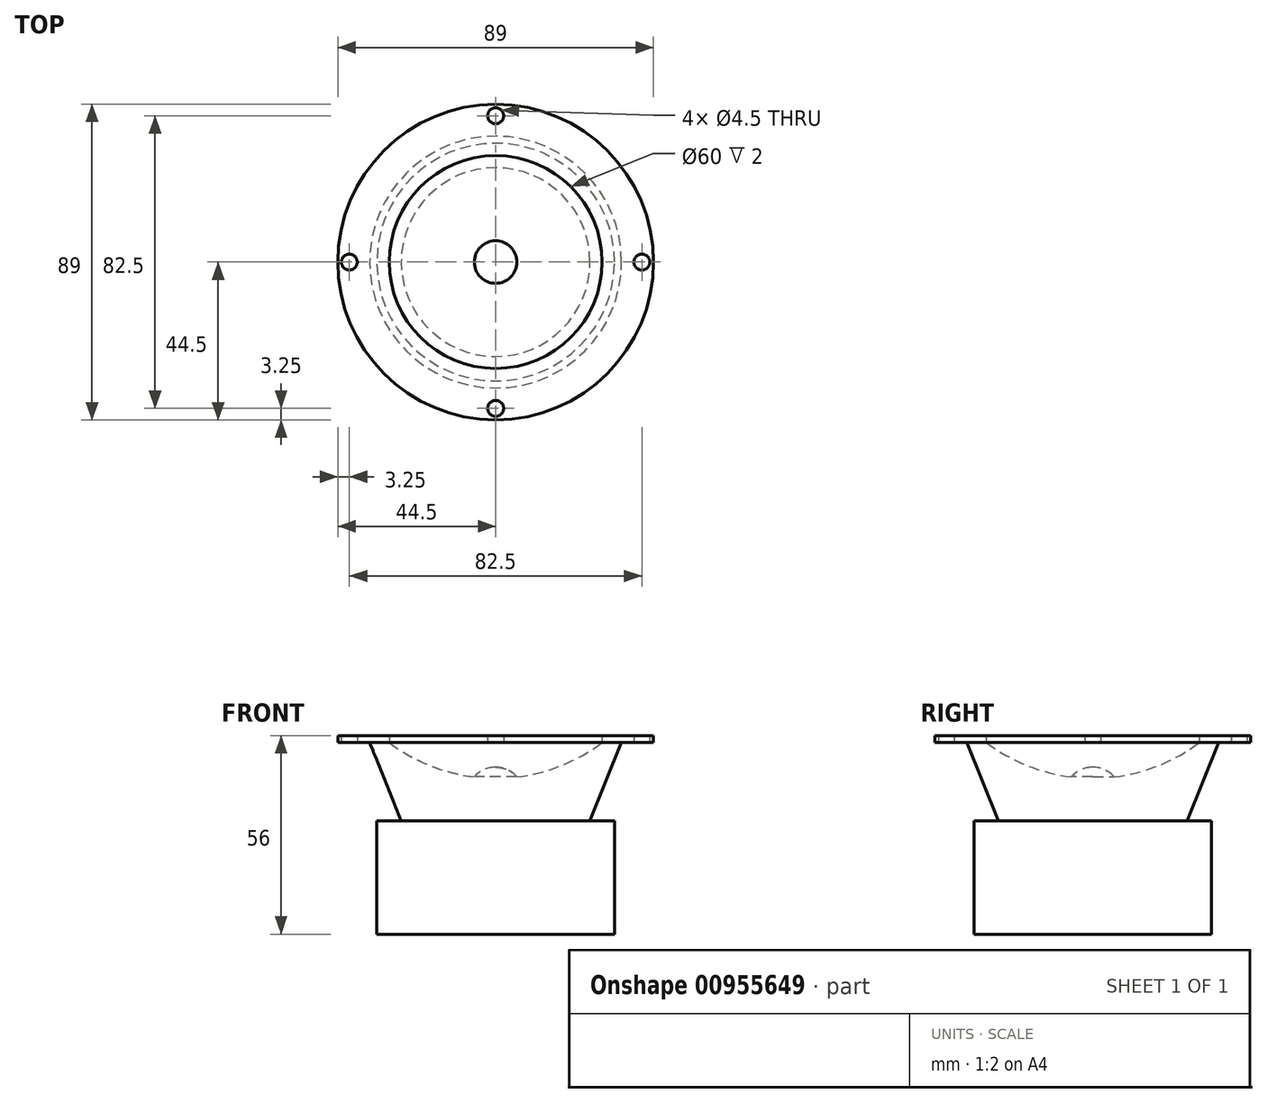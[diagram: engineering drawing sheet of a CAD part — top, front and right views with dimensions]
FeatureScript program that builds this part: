
annotation { "Feature Type Name" : "Feature", "Feature Type Description" : "" }
export const myFeature = defineFeature(function(context is Context, id is Id, definition is map)
    precondition{}
    {
        {
            var Q0;
            Q0=qCreatedBy(makeId("Top.planeOp"),FACE);
            var sketch = newSketch(context, id + "F0", { "sketchPlane" : qUnion([Q0])});
            skCircle(sketch, "E0", {"center": v(0, 0) * mm, "radius": 44.5 * mm});
            skCircle(sketch, "E1", {"center": v(0, -41.25) * mm, "radius": 2.25 * mm});
            skLineSegment(sketch, "E2", {"start": v(0, 0) * mm, "end": v(0, -41.25) * mm, "construction": true});
            skCircle(sketch, "E3.1.0", {"center": v(41.25, 0) * mm, "radius": 2.25 * mm});
            skCircle(sketch, "E3.2.0", {"center": v(0, 41.25) * mm, "radius": 2.25 * mm});
            skCircle(sketch, "E3.3.0", {"center": v(-41.25, 0) * mm, "radius": 2.25 * mm});
            skSolve(sketch);
        }
        {
            var Q0;
            Q0=makeQuery(id+"F0.imprint","IMPRINT",FACE,{"disambiguationData":[TD([[makeQuery(id+"F0.imprint","IMPRINT",EDGE,{"derivedFrom":sQuery(id+"F0.wireOp",EDGE,"E0")}),1.0]])]});
            extrude(context, id + "F1", {"entities" : qUnion([Q0]), "depth" : 2 * mm, "offsetDistance" : 25 * mm});
        }
        {
            var Q0;
            Q0=makeQuery(id+"F1.opExtrude","CAP_FACE",FACE,{"disambiguationData":[OSD([sQuery(id+"F0.wireOp",EDGE,"E0"),sQuery(id+"F0.wireOp",EDGE,"E1"),sQuery(id+"F0.wireOp",EDGE,"E3.1.0"),sQuery(id+"F0.wireOp",EDGE,"E3.2.0"),sQuery(id+"F0.wireOp",EDGE,"E3.3.0")])],"isStart":true});
            var sketch = newSketch(context, id + "F2", { "sketchPlane" : qUnion([Q0])});
            skCircle(sketch, "E4", {"center": v(0, 0) * mm, "radius": 35.5 * mm});
            skSolve(sketch);
        }
        {
            var Q0;
            Q0=makeQuery(id+"F2.imprint","IMPRINT",FACE,{"disambiguationData":[TD([[makeQuery(id+"F2.imprint","IMPRINT",EDGE,{"derivedFrom":sQuery(id+"F2.wireOp",EDGE,"E4")}),1.0]])]});
            extrude(context, id + "F3", {"entities" : qUnion([Q0]), "operationType" : NewBodyOperationType.ADD, "depth" : 22 * mm, "offsetDistance" : 25 * mm, "hasDraft" : true, "draftAngle" : 22 * degree, "draftPullDirection" : true});
        }
        {
            var Q0;
            Q0=makeQuery(id+"F3.opExtrude","CAP_FACE",FACE,{"disambiguationData":[OSD([sQuery(id+"F2.wireOp",EDGE,"E4")])],"isStart":false});
            var sketch = newSketch(context, id + "F4", { "sketchPlane" : qUnion([Q0])});
            skCircle(sketch, "E5", {"center": v(0, 0) * mm, "radius": 33.5 * mm});
            skSolve(sketch);
        }
        {
            var Q0;
            Q0=makeQuery(id+"F4.imprint","IMPRINT",FACE,{"disambiguationData":[TD([[makeQuery(id+"F4.imprint","IMPRINT",EDGE,{"derivedFrom":sQuery(id+"F4.wireOp",EDGE,"E5")}),1.0]])]});
            var Q1;
            Q1=makeQuery(id+"F4.imprint","IMPRINT",FACE,{"disambiguationData":[TD([[makeQuery(id+"F4.imprint","IMPRINT",EDGE,{"derivedFrom":makeQuery(id+"F3.opExtrude","CAP_EDGE",EDGE,{"disambiguationData":[OSD([sQuery(id+"F2.wireOp",EDGE,"E4")])],"isStart":false})}),1.0]])]});
            extrude(context, id + "F5", {"entities" : qUnion([Q0, Q1]), "operationType" : NewBodyOperationType.ADD, "depth" : 32 * mm, "offsetDistance" : 25 * mm});
        }
        {
            var Q0;
            Q0=qCreatedBy(makeId("Front.planeOp"),FACE);
            var sketch = newSketch(context, id + "F6", { "sketchPlane" : qUnion([Q0])});
            skArc(sketch, "E6", {"start": v(-30, 0) * mm, "mid": v(0, -10) * mm, "end": v(30, 0) * mm});
            skLineSegment(sketch, "E7", {"start": v(0, 0) * mm, "end": v(0, -10) * mm});
            skLineSegment(sketch, "E8", {"start": v(0, 3) * mm, "end": v(30, 3) * mm});
            skLineSegment(sketch, "E9", {"start": v(0, 3) * mm, "end": v(0, 0) * mm});
            skLineSegment(sketch, "E10", {"start": v(30, 3) * mm, "end": v(30, 0) * mm});
            skArc(sketch, "E11", {"start": v(6, -9.64) * mm, "mid": v(0, -6.93) * mm, "end": v(-6, -9.64) * mm});
            skSolve(sketch);
        }
        {
            var Q0;
            Q0=makeQuery(id+"F6.imprint","IMPRINT",FACE,{"disambiguationData":[TD([[makeQuery(id+"F6.imprint","IMPRINT",EDGE,{"derivedFrom":sQuery(id+"F6.wireOp",EDGE,"E8")}),-1.0]])]});
            var Q1;
            Q1=sQuery(id+"F6.wireOp",EDGE,"E7");
            revolve(context, id + "F7", {"operationType" : NewBodyOperationType.REMOVE, "surfaceOperationType" : NewSurfaceOperationType.NEW, "entities" : qUnion([Q0]), "axis" : qUnion([Q1]), "revolveType" : RevolveType.FULL, "oppositeDirection" : true});
        }
    });
